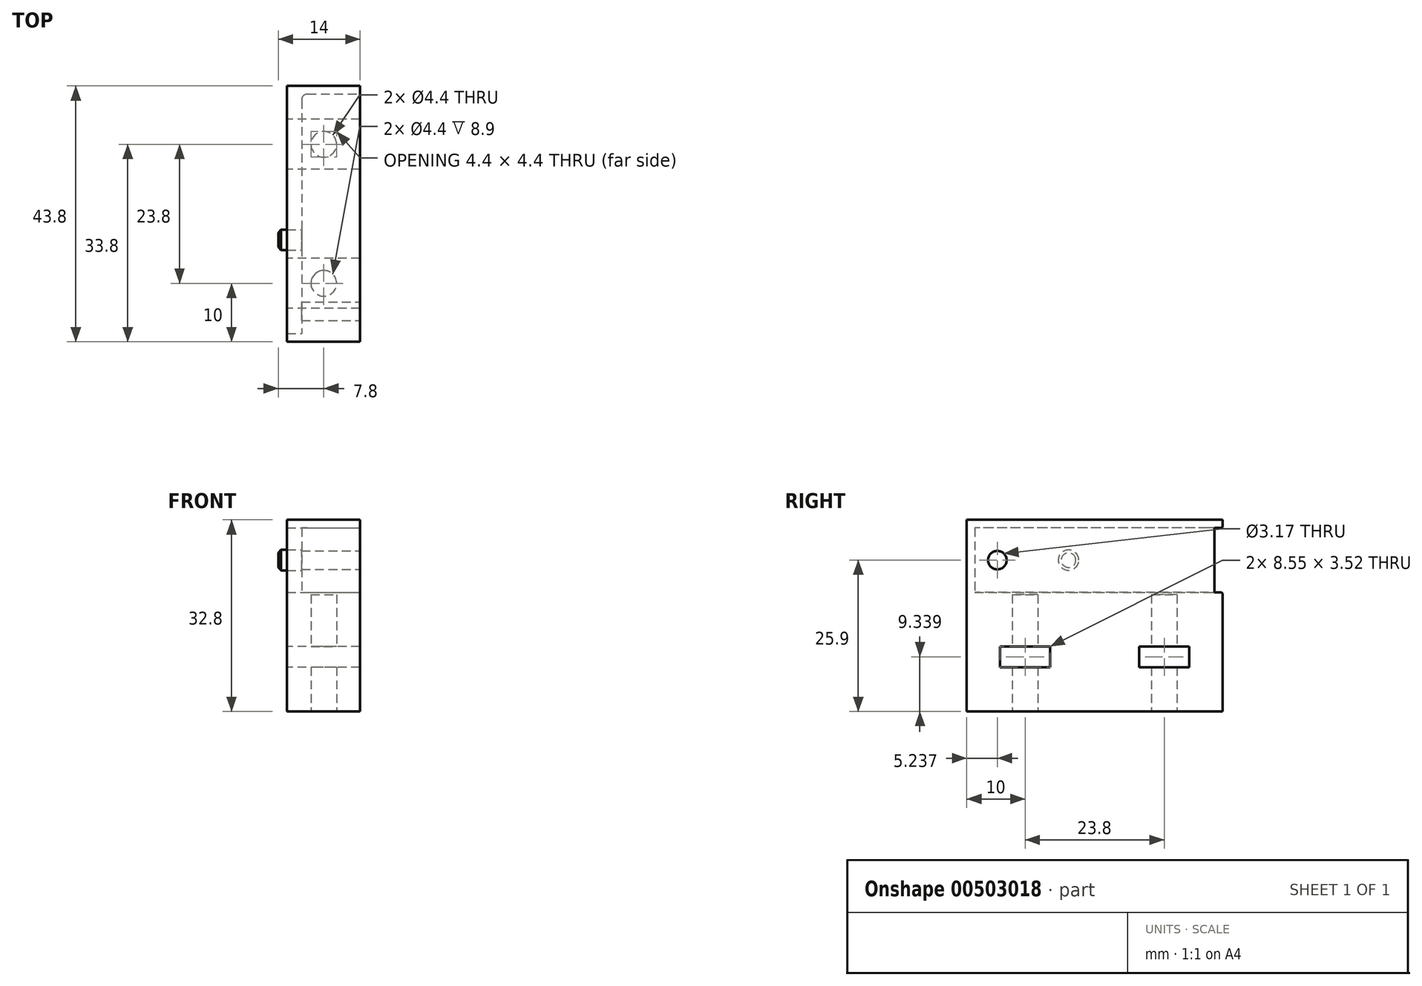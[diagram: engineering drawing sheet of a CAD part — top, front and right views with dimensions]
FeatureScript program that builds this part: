
annotation { "Feature Type Name" : "Feature", "Feature Type Description" : "" }
export const myFeature = defineFeature(function(context is Context, id is Id, definition is map)
    precondition{}
    {
        {
            var Q0;
            Q0=qCreatedBy(makeId("Right.planeOp"),FACE);
            var sketch = newSketch(context, id + "F0", { "sketchPlane" : qUnion([Q0])});
            skLineSegment(sketch, "E0.bottom", {"start": v(20.5, 5.5) * mm, "end": v(-20.5, 5.5) * mm});
            skLineSegment(sketch, "E0.top", {"start": v(20.5, -5.5) * mm, "end": v(-20.5, -5.5) * mm});
            skLineSegment(sketch, "E0.left", {"start": v(20.5, 5.5) * mm, "end": v(20.5, -5.5) * mm});
            skLineSegment(sketch, "E0.right", {"start": v(-20.5, 5.5) * mm, "end": v(-20.5, -5.5) * mm});
            skPoint(sketch, "E0.middle", {"position": v(0, 0) * mm});
            skLineSegment(sketch, "E1.0", {"start": v(21.9, 6.9) * mm, "end": v(21.9, 5.83) * mm});
            skLineSegment(sketch, "E1.1", {"start": v(21.9, 6.9) * mm, "end": v(-21.9, 6.9) * mm});
            skLineSegment(sketch, "E1.2", {"start": v(-21.9, 6.9) * mm, "end": v(-21.9, -6.9) * mm});
            skLineSegment(sketch, "E1.3", {"start": v(21.9, -6.9) * mm, "end": v(-21.9, -6.9) * mm});
            skCircle(sketch, "E2", {"center": v(-16.66, 0) * mm, "radius": 1.59 * mm});
            skCircle(sketch, "E3", {"center": v(-4.47, 0) * mm, "radius": 1.75 * mm});
            skLineSegment(sketch, "E4", {"start": v(20.5, 5.5) * mm, "end": v(21.57, 5.5) * mm});
            skLineSegment(sketch, "E5", {"start": v(20.5, -5.5) * mm, "end": v(21.57, -5.5) * mm});
            skLineSegment(sketch, "E6.trimOffspring", {"start": v(21.9, -5.83) * mm, "end": v(21.9, -6.9) * mm});
            skPoint(sketch, "E7.visualSharp", {"position": v(21.9, 5.5) * mm});
            skArc(sketch, "E7.filletArc", {"start": v(21.57, 5.5) * mm, "mid": v(21.8, 5.6) * mm, "end": v(21.9, 5.83) * mm});
            skPoint(sketch, "E8.visualSharp", {"position": v(21.9, -5.5) * mm});
            skArc(sketch, "E8.filletArc", {"start": v(21.9, -5.83) * mm, "mid": v(21.8, -5.6) * mm, "end": v(21.57, -5.5) * mm});
            skSolve(sketch);
        }
        {
            var Q0;
            Q0=makeQuery(id+"F0.imprint","IMPRINT",FACE,{"disambiguationData":[TD([[makeQuery(id+"F0.imprint","IMPRINT",EDGE,{"derivedFrom":sQuery(id+"F0.wireOp",EDGE,"E0.bottom")}),1.0]])]});
            extrude(context, id + "F1", {"entities" : qUnion([Q0]), "oppositeDirection" : true, "depth" : 10 * mm});
        }
        {
            var Q0;
            Q0=makeQuery(id+"F0.imprint","IMPRINT",FACE,{"disambiguationData":[TD([[makeQuery(id+"F0.imprint","IMPRINT",EDGE,{"derivedFrom":sQuery(id+"F0.wireOp",EDGE,"E0.bottom")}),-1.0]])]});
            extrude(context, id + "F2", {"entities" : qUnion([Q0]), "operationType" : NewBodyOperationType.ADD, "oppositeDirection" : true, "depth" : 12.5 * mm});
        }
        {
            var Q0;
            Q0=makeQuery(id+"F1.opExtrude","CAP_EDGE",EDGE,{"disambiguationData":[OSD([sQuery(id+"F0.wireOp",EDGE,"E0.bottom")])],"isStart":false});
            var Q1;
            Q1=makeQuery(id+"F1.opExtrude","CAP_EDGE",EDGE,{"disambiguationData":[OSD([sQuery(id+"F0.wireOp",EDGE,"E0.right")])],"isStart":false});
            var Q2;
            Q2=makeQuery(id+"F1.opExtrude","CAP_EDGE",EDGE,{"disambiguationData":[OSD([sQuery(id+"F0.wireOp",EDGE,"E0.top")])],"isStart":false});
            var Q3;
            Q3=makeQuery(id+"F1.opExtrude","CAP_EDGE",EDGE,{"disambiguationData":[OSD([sQuery(id+"F0.wireOp",EDGE,"E0.left")])],"isStart":false});
            fillet(context, id + "F3", {"entities" : qUnion([Q0, Q1, Q2, Q3]), "radius" : 1 * mm, "tangentPropagation" : true, "allowEdgeOverflow" : false});
        }
        {
            var Q0;
            Q0=makeQuery(id+"F0.imprint","IMPRINT",FACE,{"disambiguationData":[TD([[makeQuery(id+"F0.imprint","IMPRINT",EDGE,{"derivedFrom":sQuery(id+"F0.wireOp",EDGE,"E3")}),1.0]])]});
            extrude(context, id + "F4", {"entities" : qUnion([Q0]), "operationType" : NewBodyOperationType.ADD, "oppositeDirection" : true, "depth" : 14 * mm});
        }
        {
            var Q0;
            Q0=makeQuery(id+"F4.opExtrude","CAP_FACE",FACE,{"disambiguationData":[OSD([sQuery(id+"F0.wireOp",EDGE,"E3")])],"isStart":false});
            chamfer(context, id + "F5", {"entities" : qUnion([Q0]), "width" : 0.5 * mm, "tangentPropagation" : true});
        }
        {
            var Q0;
            Q0=makeQuery(id+"F2.opExtrude","SWEPT_FACE",FACE,{"disambiguationData":[OSD([sQuery(id+"F0.wireOp",EDGE,"E1.3")])]});
            extrude(context, id + "F6", {"entities" : qUnion([Q0]), "operationType" : NewBodyOperationType.ADD, "depth" : 19 * mm});
        }
        {
            var Q0;
            Q0=makeQuery(id+"F6.opExtrude","CAP_FACE",FACE,{"disambiguationData":[OSD([sQuery(id+"F0.wireOp",EDGE,"E1.3")])],"isStart":false});
            var sketch = newSketch(context, id + "F7", { "sketchPlane" : qUnion([Q0])});
            skCircle(sketch, "E9", {"center": v(-6.2, 11.9) * mm, "radius": 2.2 * mm});
            skPoint(sketch, "E9.centerSnap0", {"position": v(-6.25, 21.9) * mm});
            skCircle(sketch, "E10", {"center": v(-6.2, -11.9) * mm, "radius": 2.2 * mm});
            skPoint(sketch, "E10.centerSnap0", {"position": v(0, 0) * mm});
            skLineSegment(sketch, "E11.0.0", {"start": v(0, -21.9) * mm, "end": v(0, 21.9) * mm, "construction": true});
            skLineSegment(sketch, "E11.0.1", {"start": v(0, 21.9) * mm, "end": v(-12.5, 21.9) * mm, "construction": true});
            skLineSegment(sketch, "E11.0.2", {"start": v(-12.5, 21.9) * mm, "end": v(-12.5, -21.9) * mm, "construction": true});
            skLineSegment(sketch, "E11.0.3", {"start": v(-12.5, -21.9) * mm, "end": v(0, -21.9) * mm, "construction": true});
            skSolve(sketch);
        }
        {
            var Q0;
            Q0=makeQuery(id+"F7.imprint","IMPRINT",FACE,{"disambiguationData":[TD([[makeQuery(id+"F7.imprint","IMPRINT",EDGE,{"derivedFrom":sQuery(id+"F7.wireOp",EDGE,"E9")}),1.0]])]});
            var Q1;
            Q1=makeQuery(id+"F7.imprint","IMPRINT",FACE,{"disambiguationData":[TD([[makeQuery(id+"F7.imprint","IMPRINT",EDGE,{"derivedFrom":sQuery(id+"F7.wireOp",EDGE,"E10")}),1.0]])]});
            extrude(context, id + "F8", {"entities" : qUnion([Q0, Q1]), "operationType" : NewBodyOperationType.REMOVE, "oppositeDirection" : true, "depth" : 20 * mm});
        }
        {
            var Q0;
            {var subQ0=sQuery(id+"F0.wireOp",EDGE,"E1.3");Q0=makeQuery(id+"F6.boolean.opBoolean","MERGE",FACE,{"derivedFrom":[makeQuery(id+"F2.opExtrude","CAP_FACE",FACE,{"disambiguationData":[OSD([sQuery(id+"F0.wireOp",EDGE,"E0.bottom"),sQuery(id+"F0.wireOp",EDGE,"E0.top"),sQuery(id+"F0.wireOp",EDGE,"E0.left"),sQuery(id+"F0.wireOp",EDGE,"E0.right"),sQuery(id+"F0.wireOp",EDGE,"E1.0"),sQuery(id+"F0.wireOp",EDGE,"E1.1"),sQuery(id+"F0.wireOp",EDGE,"E1.2"),subQ0])],"isStart":false}),makeQuery(id+"F6.opExtrude","SWEPT_FACE",FACE,{"disambiguationData":[OSD([subQ0]),TDD([makeQuery(id+"F2.opExtrude","CAP_EDGE",EDGE,{"disambiguationData":[OSD([subQ0])],"isStart":false})])]})]});}
            var sketch = newSketch(context, id + "F9", { "sketchPlane" : qUnion([Q0])});
            skLineSegment(sketch, "E12.bottom", {"start": v(-7.63, -18.32) * mm, "end": v(-16.18, -18.32) * mm});
            skLineSegment(sketch, "E12.top", {"start": v(-7.63, -14.8) * mm, "end": v(-16.18, -14.8) * mm});
            skLineSegment(sketch, "E12.left", {"start": v(-7.63, -18.32) * mm, "end": v(-7.63, -14.8) * mm});
            skLineSegment(sketch, "E12.right", {"start": v(-16.18, -18.32) * mm, "end": v(-16.18, -14.8) * mm});
            skPoint(sketch, "E12.middle", {"position": v(-11.9, -16.56) * mm});
            skLineSegment(sketch, "E13.0", {"start": v(-9.7, -5.9) * mm, "end": v(-14.1, -5.9) * mm, "construction": true});
            skPoint(sketch, "E14", {"position": v(-11.9, -5.9) * mm});
            skLineSegment(sketch, "E15.MirrorCS", {"start": v(7.63, -14.8) * mm, "end": v(16.18, -14.8) * mm});
            skLineSegment(sketch, "E16.MirrorCS", {"start": v(16.18, -18.32) * mm, "end": v(16.18, -14.8) * mm});
            skLineSegment(sketch, "E17.MirrorCS", {"start": v(7.63, -18.32) * mm, "end": v(16.18, -18.32) * mm});
            skLineSegment(sketch, "E18.MirrorCS", {"start": v(7.63, -18.32) * mm, "end": v(7.63, -14.8) * mm});
            skSolve(sketch);
        }
        {
            var Q0;
            Q0=makeQuery(id+"F9.imprint","IMPRINT",FACE,{"disambiguationData":[TD([[makeQuery(id+"F9.imprint","IMPRINT",EDGE,{"derivedFrom":sQuery(id+"F9.wireOp",EDGE,"E12.bottom")}),-1.0]])]});
            var Q1;
            Q1=makeQuery(id+"F9.imprint","IMPRINT",FACE,{"disambiguationData":[TD([[makeQuery(id+"F9.imprint","IMPRINT",EDGE,{"derivedFrom":sQuery(id+"F9.wireOp",EDGE,"E15.MirrorCS")}),-1.0]])]});
            extrude(context, id + "F10", {"entities" : qUnion([Q0, Q1]), "operationType" : NewBodyOperationType.REMOVE, "oppositeDirection" : true, "depth" : 22.3 * mm});
        }
    });
